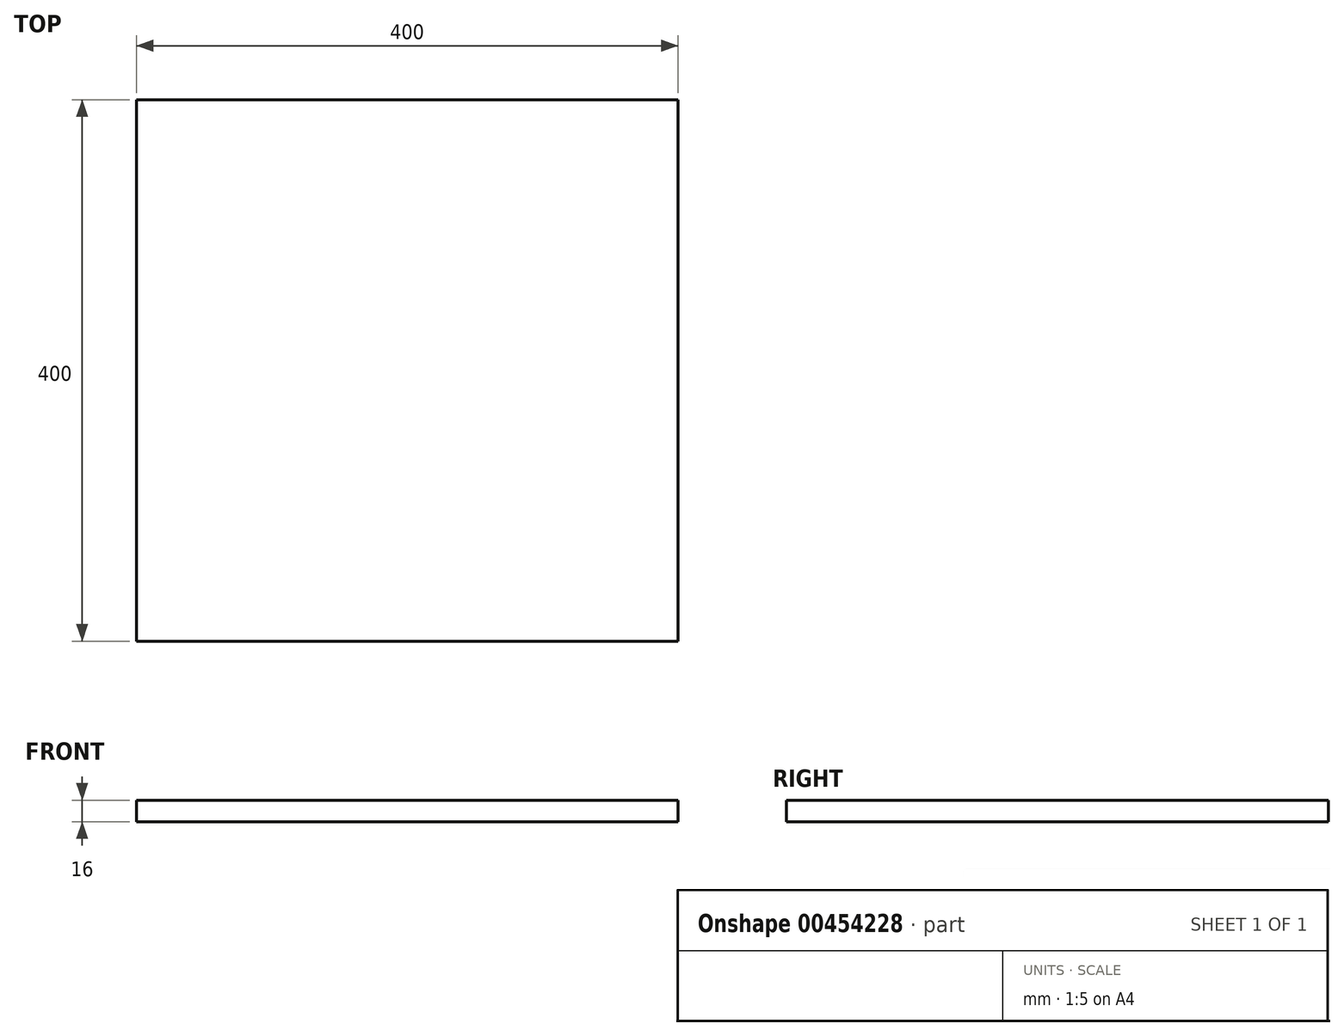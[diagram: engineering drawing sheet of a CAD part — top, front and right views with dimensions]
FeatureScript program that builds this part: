
annotation { "Feature Type Name" : "Feature", "Feature Type Description" : "" }
export const myFeature = defineFeature(function(context is Context, id is Id, definition is map)
    precondition{}
    {
        {
            var Q0;
            Q0=qCreatedBy(makeId("Top.planeOp"),FACE);
            var sketch = newSketch(context, id + "F0", { "sketchPlane" : qUnion([Q0])});
            skLineSegment(sketch, "E0.bottom", {"start": v(200, -200) * mm, "end": v(-200, -200) * mm});
            skLineSegment(sketch, "E0.top", {"start": v(200, 200) * mm, "end": v(-200, 200) * mm});
            skLineSegment(sketch, "E0.left", {"start": v(200, -200) * mm, "end": v(200, 200) * mm});
            skLineSegment(sketch, "E0.right", {"start": v(-200, -200) * mm, "end": v(-200, 200) * mm});
            skPoint(sketch, "E0.middle", {"position": v(0, 0) * mm});
            skSolve(sketch);
        }
        {
            var Q0;
            Q0 = qSketchRegion(id + "F0", true);
            extrude(context, id + "F1", {"entities" : qUnion([Q0]), "depth" : 16 * mm});
        }
    });
